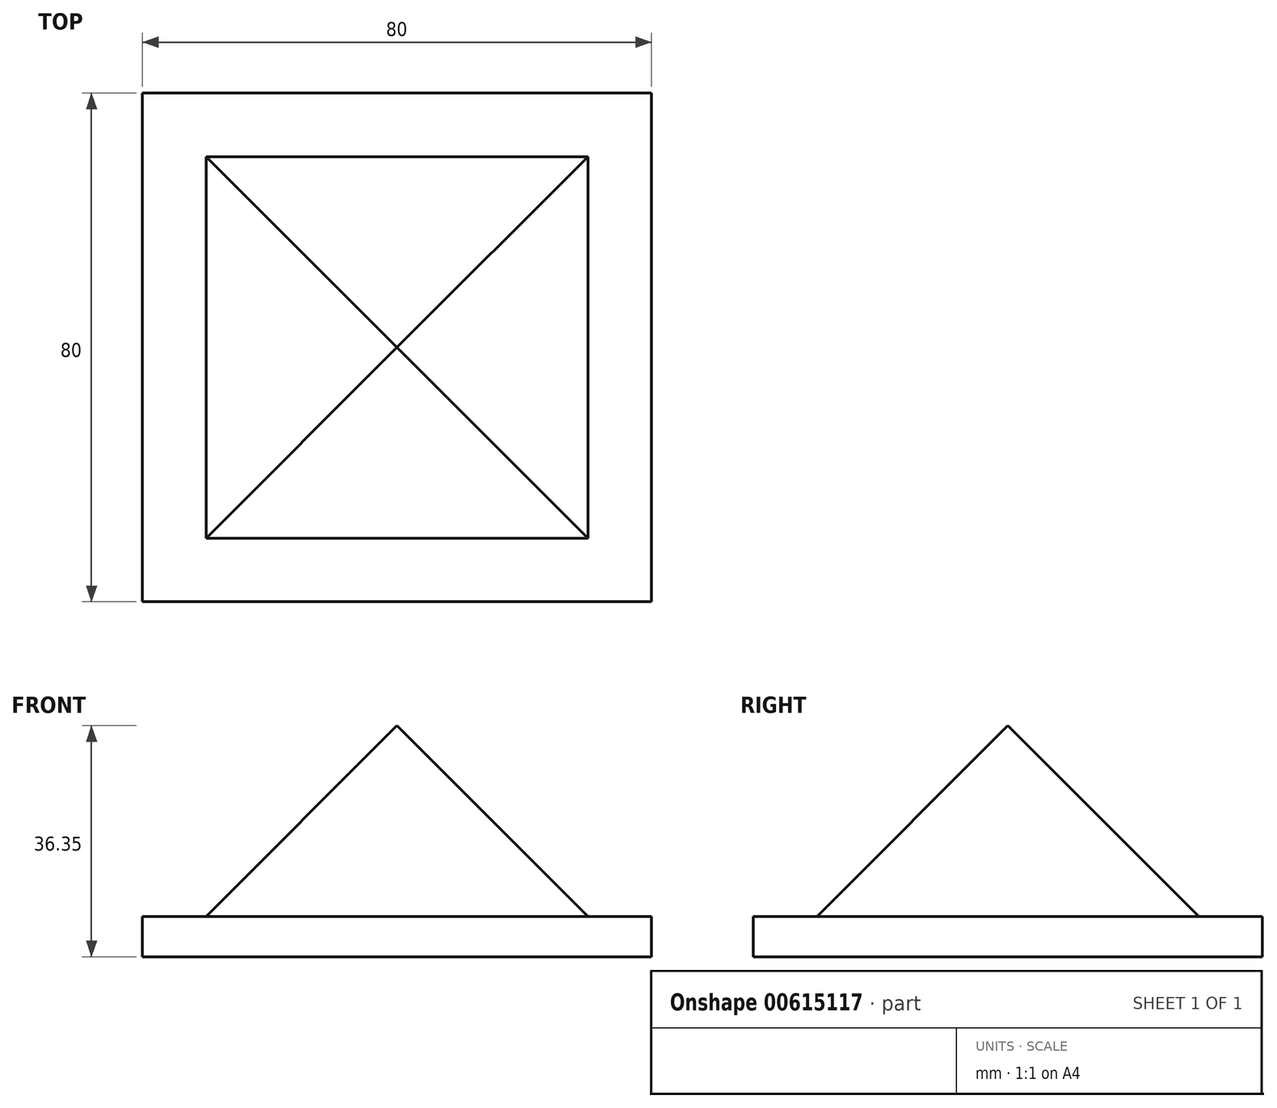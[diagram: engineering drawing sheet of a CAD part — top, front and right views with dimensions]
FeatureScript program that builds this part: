
annotation { "Feature Type Name" : "Feature", "Feature Type Description" : "" }
export const myFeature = defineFeature(function(context is Context, id is Id, definition is map)
    precondition{}
    {
        {
            var Q0;
            Q0=qCreatedBy(makeId("Top.planeOp"),FACE);
            var sketch = newSketch(context, id + "F0", { "sketchPlane" : qUnion([Q0])});
            skLineSegment(sketch, "E0.bottom", {"start": v(30, -30) * mm, "end": v(-30, -30) * mm});
            skLineSegment(sketch, "E0.top", {"start": v(30, 30) * mm, "end": v(-30, 30) * mm});
            skLineSegment(sketch, "E0.left", {"start": v(30, -30) * mm, "end": v(30, 30) * mm});
            skLineSegment(sketch, "E0.right", {"start": v(-30, -30) * mm, "end": v(-30, 30) * mm});
            skPoint(sketch, "E0.middle", {"position": v(0, 0) * mm});
            skSolve(sketch);
        }
        {
            var Q0;
            Q0 = qSketchRegion(id + "F0", true);
            extrude(context, id + "F1", {"entities" : qUnion([Q0]), "depth" : 30 * mm, "offsetDistance" : 25 * mm, "hasDraft" : true, "draftAngle" : 45 * degree, "draftPullDirection" : true});
        }
        {
            var Q0;
            Q0=makeQuery(id+"F1.opExtrude","CAP_FACE",FACE,{"disambiguationData":[OSD([sQuery(id+"F0.wireOp",EDGE,"E0.bottom"),sQuery(id+"F0.wireOp",EDGE,"E0.top"),sQuery(id+"F0.wireOp",EDGE,"E0.left"),sQuery(id+"F0.wireOp",EDGE,"E0.right")])],"isStart":true});
            var sketch = newSketch(context, id + "F2", { "sketchPlane" : qUnion([Q0])});
            skLineSegment(sketch, "E1.bottom", {"start": v(40, -40) * mm, "end": v(-40, -40) * mm});
            skLineSegment(sketch, "E1.top", {"start": v(40, 40) * mm, "end": v(-40, 40) * mm});
            skLineSegment(sketch, "E1.left", {"start": v(40, -40) * mm, "end": v(40, 40) * mm});
            skLineSegment(sketch, "E1.right", {"start": v(-40, -40) * mm, "end": v(-40, 40) * mm});
            skPoint(sketch, "E1.middle", {"position": v(0, 0) * mm});
            skSolve(sketch);
        }
        {
            var Q0;
            Q0=makeQuery(id+"F2.imprint","IMPRINT",FACE,{"disambiguationData":[TD([[makeQuery(id+"F2.imprint","IMPRINT",EDGE,{"derivedFrom":makeQuery(id+"F1.opExtrude","CAP_EDGE",EDGE,{"disambiguationData":[OSD([sQuery(id+"F0.wireOp",EDGE,"E0.bottom")])],"isStart":true})}),1.0]])]});
            var Q1;
            Q1=makeQuery(id+"F2.imprint","IMPRINT",FACE,{"disambiguationData":[TD([[makeQuery(id+"F2.imprint","IMPRINT",EDGE,{"derivedFrom":sQuery(id+"F2.wireOp",EDGE,"E1.bottom")}),-1.0]])]});
            extrude(context, id + "F3", {"entities" : qUnion([Q0, Q1]), "operationType" : NewBodyOperationType.ADD, "depth" : 6.35 * mm, "offsetDistance" : 25 * mm});
        }
    });
